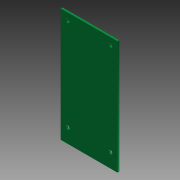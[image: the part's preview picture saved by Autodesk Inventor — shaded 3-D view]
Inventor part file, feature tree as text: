
AUTODESK INVENTOR PART (.ipt)
format: ipt  version: 2012 (Build 160160000, 160)  size: 92,672 bytes
history: native  units: in
note: dims shown in document units (in); Inventor stores cm internally (conversion verified against a paired STEP export)
features: extrude x2, sketch x2
ambient origin geometry x8: Origin, YZ Plane, XZ Plane, XY Plane, X Axis, Y Axis, Z Axis, Center Point
bodies: Solid1 (feature_tree)
feature tree (4):
  extrude  "Extrusion1"  Depth=2.0in
  extrude  "Extrusion2"  Depth=0.129in
  sketch  "Sketch1"  dims[d0=0.063in d1=0.0in d2=2.0in]
  sketch  "Sketch2"  dims[d3=4.0in d4=0.129in d5=0.7874in d7=3.25in d8=0.7874in d10=1.5in d13=0.25in d14=0.5in d15=0.0157in d16=0.0in d17=0.0295in d20=3.44in d21=0.54in d22=0.1in d23=0.1in]
